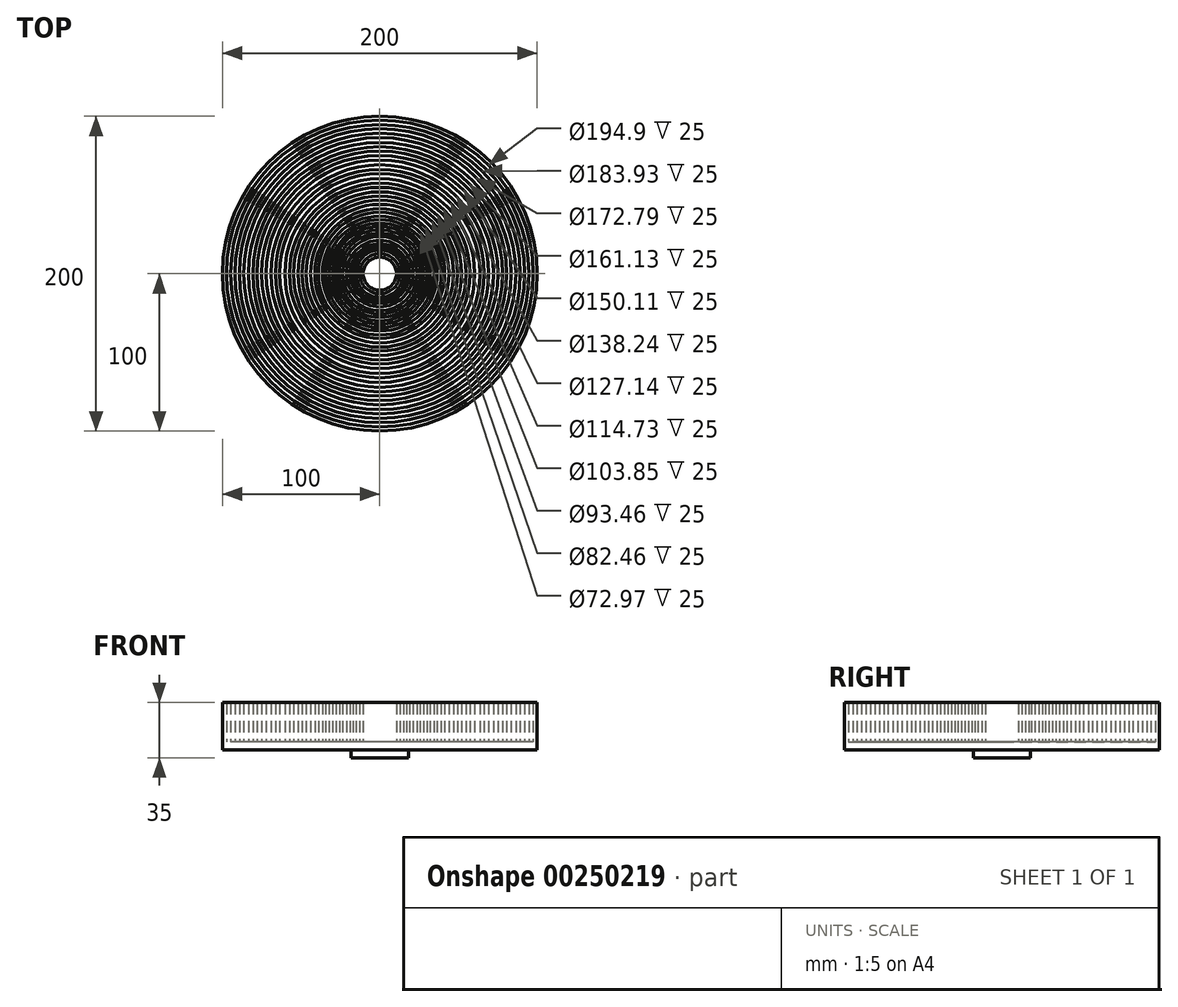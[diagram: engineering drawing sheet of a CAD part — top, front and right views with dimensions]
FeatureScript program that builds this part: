
annotation { "Feature Type Name" : "Feature", "Feature Type Description" : "" }
export const myFeature = defineFeature(function(context is Context, id is Id, definition is map)
    precondition{}
    {
        {
            var Q0;
            Q0=qCreatedBy(makeId("Top.planeOp"),FACE);
            var sketch = newSketch(context, id + "F0", { "sketchPlane" : qUnion([Q0])});
            skCircle(sketch, "E0", {"center": v(0, 0) * mm, "radius": 100 * mm});
            skSolve(sketch);
        }
        {
            var Q0;
            Q0=makeQuery(id+"F0.imprint","IMPRINT",FACE,{"disambiguationData":[TD([[makeQuery(id+"F0.imprint","IMPRINT",EDGE,{"derivedFrom":sQuery(id+"F0.wireOp",EDGE,"E0")}),1.0]])]});
            extrude(context, id + "F1", {"entities" : qUnion([Q0]), "depth" : 5 * mm});
        }
        {
            var Q0;
            Q0=makeQuery(id+"F1.opExtrude","CAP_FACE",FACE,{"disambiguationData":[OSD([sQuery(id+"F0.wireOp",EDGE,"E0")])],"isStart":false});
            var sketch = newSketch(context, id + "F2", { "sketchPlane" : qUnion([Q0])});
            skCircle(sketch, "E1", {"center": v(0, 0) * mm, "radius": 97.45 * mm});
            skCircle(sketch, "E2", {"center": v(0, 0) * mm, "radius": 94.65 * mm});
            skCircle(sketch, "E3", {"center": v(0, 0) * mm, "radius": 91.97 * mm});
            skCircle(sketch, "E4", {"center": v(0, 0) * mm, "radius": 89.15 * mm});
            skCircle(sketch, "E5", {"center": v(0, 0) * mm, "radius": 86.4 * mm});
            skCircle(sketch, "E6", {"center": v(0, 0) * mm, "radius": 83.36 * mm});
            skCircle(sketch, "E7", {"center": v(0, 0) * mm, "radius": 80.56 * mm});
            skCircle(sketch, "E8", {"center": v(0, 0) * mm, "radius": 77.88 * mm});
            skCircle(sketch, "E9", {"center": v(0, 0) * mm, "radius": 75.05 * mm});
            skCircle(sketch, "E10", {"center": v(0, 0) * mm, "radius": 72.25 * mm});
            skCircle(sketch, "E11", {"center": v(0, 0) * mm, "radius": 69.12 * mm});
            skCircle(sketch, "E12", {"center": v(0, 0) * mm, "radius": 66.16 * mm});
            skCircle(sketch, "E13", {"center": v(0, 0) * mm, "radius": 63.57 * mm});
            skCircle(sketch, "E14", {"center": v(0, 0) * mm, "radius": 60.3 * mm});
            skCircle(sketch, "E15", {"center": v(0, 0) * mm, "radius": 57.37 * mm});
            skCircle(sketch, "E16", {"center": v(0, 0) * mm, "radius": 54.8 * mm});
            skCircle(sketch, "E17", {"center": v(0, 0) * mm, "radius": 51.92 * mm});
            skCircle(sketch, "E18", {"center": v(0, 0) * mm, "radius": 49.27 * mm});
            skCircle(sketch, "E19", {"center": v(0, 0) * mm, "radius": 46.73 * mm});
            skCircle(sketch, "E20", {"center": v(0, 0) * mm, "radius": 43.96 * mm});
            skCircle(sketch, "E21", {"center": v(0, 0) * mm, "radius": 41.23 * mm});
            skCircle(sketch, "E22", {"center": v(0, 0) * mm, "radius": 39.03 * mm});
            skCircle(sketch, "E23", {"center": v(0, 0) * mm, "radius": 36.49 * mm});
            skCircle(sketch, "E24", {"center": v(0, 0) * mm, "radius": 34.31 * mm});
            skCircle(sketch, "E25", {"center": v(0, 0) * mm, "radius": 32.07 * mm});
            skCircle(sketch, "E26", {"center": v(0, 0) * mm, "radius": 29.96 * mm});
            skCircle(sketch, "E27", {"center": v(0, 0) * mm, "radius": 27.78 * mm});
            skCircle(sketch, "E28", {"center": v(0, 0) * mm, "radius": 25.7 * mm});
            skCircle(sketch, "E29", {"center": v(0, 0) * mm, "radius": 23.57 * mm});
            skCircle(sketch, "E30", {"center": v(0, 0) * mm, "radius": 21.15 * mm});
            skCircle(sketch, "E31", {"center": v(0, 0) * mm, "radius": 18.93 * mm});
            skCircle(sketch, "E32", {"center": v(0, 0) * mm, "radius": 17.04 * mm});
            skCircle(sketch, "E33", {"center": v(0, 0) * mm, "radius": 15.09 * mm});
            skCircle(sketch, "E34", {"center": v(0, 0) * mm, "radius": 12.77 * mm});
            skCircle(sketch, "E35", {"center": v(0, 0) * mm, "radius": 10.55 * mm});
            skSolve(sketch);
        }
        {
            var Q0;
            Q0=makeQuery(id+"F2.imprint","IMPRINT",FACE,{"disambiguationData":[TD([[makeQuery(id+"F2.imprint","IMPRINT",EDGE,{"derivedFrom":sQuery(id+"F2.wireOp",EDGE,"E1")}),-1.0]])]});
            var Q1;
            Q1=makeQuery(id+"F2.imprint","IMPRINT",FACE,{"disambiguationData":[TD([[makeQuery(id+"F2.imprint","IMPRINT",EDGE,{"derivedFrom":sQuery(id+"F2.wireOp",EDGE,"E2")}),1.0]])]});
            var Q2;
            Q2=makeQuery(id+"F2.imprint","IMPRINT",FACE,{"disambiguationData":[TD([[makeQuery(id+"F2.imprint","IMPRINT",EDGE,{"derivedFrom":sQuery(id+"F2.wireOp",EDGE,"E4")}),1.0]])]});
            var Q3;
            Q3=makeQuery(id+"F2.imprint","IMPRINT",FACE,{"disambiguationData":[TD([[makeQuery(id+"F2.imprint","IMPRINT",EDGE,{"derivedFrom":sQuery(id+"F2.wireOp",EDGE,"E6")}),1.0]])]});
            var Q4;
            Q4=makeQuery(id+"F2.imprint","IMPRINT",FACE,{"disambiguationData":[TD([[makeQuery(id+"F2.imprint","IMPRINT",EDGE,{"derivedFrom":sQuery(id+"F2.wireOp",EDGE,"E8")}),1.0]])]});
            var Q5;
            Q5=makeQuery(id+"F2.imprint","IMPRINT",FACE,{"disambiguationData":[TD([[makeQuery(id+"F2.imprint","IMPRINT",EDGE,{"derivedFrom":sQuery(id+"F2.wireOp",EDGE,"E10")}),1.0]])]});
            var Q6;
            Q6=makeQuery(id+"F2.imprint","IMPRINT",FACE,{"disambiguationData":[TD([[makeQuery(id+"F2.imprint","IMPRINT",EDGE,{"derivedFrom":sQuery(id+"F2.wireOp",EDGE,"E12")}),1.0]])]});
            var Q7;
            Q7=makeQuery(id+"F2.imprint","IMPRINT",FACE,{"disambiguationData":[TD([[makeQuery(id+"F2.imprint","IMPRINT",EDGE,{"derivedFrom":sQuery(id+"F2.wireOp",EDGE,"E14")}),1.0]])]});
            var Q8;
            Q8=makeQuery(id+"F2.imprint","IMPRINT",FACE,{"disambiguationData":[TD([[makeQuery(id+"F2.imprint","IMPRINT",EDGE,{"derivedFrom":sQuery(id+"F2.wireOp",EDGE,"E16")}),1.0]])]});
            var Q9;
            Q9=makeQuery(id+"F2.imprint","IMPRINT",FACE,{"disambiguationData":[TD([[makeQuery(id+"F2.imprint","IMPRINT",EDGE,{"derivedFrom":sQuery(id+"F2.wireOp",EDGE,"E18")}),1.0]])]});
            var Q10;
            Q10=makeQuery(id+"F2.imprint","IMPRINT",FACE,{"disambiguationData":[TD([[makeQuery(id+"F2.imprint","IMPRINT",EDGE,{"derivedFrom":sQuery(id+"F2.wireOp",EDGE,"E20")}),1.0]])]});
            var Q11;
            Q11=makeQuery(id+"F2.imprint","IMPRINT",FACE,{"disambiguationData":[TD([[makeQuery(id+"F2.imprint","IMPRINT",EDGE,{"derivedFrom":sQuery(id+"F2.wireOp",EDGE,"E22")}),1.0]])]});
            var Q12;
            Q12=makeQuery(id+"F2.imprint","IMPRINT",FACE,{"disambiguationData":[TD([[makeQuery(id+"F2.imprint","IMPRINT",EDGE,{"derivedFrom":sQuery(id+"F2.wireOp",EDGE,"E24")}),1.0]])]});
            var Q13;
            Q13=makeQuery(id+"F2.imprint","IMPRINT",FACE,{"disambiguationData":[TD([[makeQuery(id+"F2.imprint","IMPRINT",EDGE,{"derivedFrom":sQuery(id+"F2.wireOp",EDGE,"E26")}),1.0]])]});
            var Q14;
            Q14=makeQuery(id+"F2.imprint","IMPRINT",FACE,{"disambiguationData":[TD([[makeQuery(id+"F2.imprint","IMPRINT",EDGE,{"derivedFrom":sQuery(id+"F2.wireOp",EDGE,"E28")}),1.0]])]});
            var Q15;
            Q15=makeQuery(id+"F2.imprint","IMPRINT",FACE,{"disambiguationData":[TD([[makeQuery(id+"F2.imprint","IMPRINT",EDGE,{"derivedFrom":sQuery(id+"F2.wireOp",EDGE,"E30")}),1.0]])]});
            var Q16;
            Q16=makeQuery(id+"F2.imprint","IMPRINT",FACE,{"disambiguationData":[TD([[makeQuery(id+"F2.imprint","IMPRINT",EDGE,{"derivedFrom":sQuery(id+"F2.wireOp",EDGE,"E32")}),1.0]])]});
            var Q17;
            Q17=makeQuery(id+"F2.imprint","IMPRINT",FACE,{"disambiguationData":[TD([[makeQuery(id+"F2.imprint","IMPRINT",EDGE,{"derivedFrom":sQuery(id+"F2.wireOp",EDGE,"E34")}),1.0]])]});
            extrude(context, id + "F3", {"entities" : qUnion([Q0, Q1, Q2, Q3, Q4, Q5, Q6, Q7, Q8, Q9, Q10, Q11, Q12, Q13, Q14, Q15, Q16, Q17]), "operationType" : NewBodyOperationType.ADD, "depth" : 25 * mm});
        }
        {
            var Q0;
            Q0=makeQuery(id+"F1.opExtrude","CAP_FACE",FACE,{"disambiguationData":[OSD([sQuery(id+"F0.wireOp",EDGE,"E0")])],"isStart":true});
            var sketch = newSketch(context, id + "F4", { "sketchPlane" : qUnion([Q0])});
            skCircle(sketch, "E36", {"center": v(0, 0) * mm, "radius": 18.2 * mm});
            skSolve(sketch);
        }
        {
            var Q0;
            Q0 = qSketchRegion(id + "F4", true);
            extrude(context, id + "F5", {"entities" : qUnion([Q0]), "operationType" : NewBodyOperationType.ADD, "depth" : 5 * mm});
        }
    });
